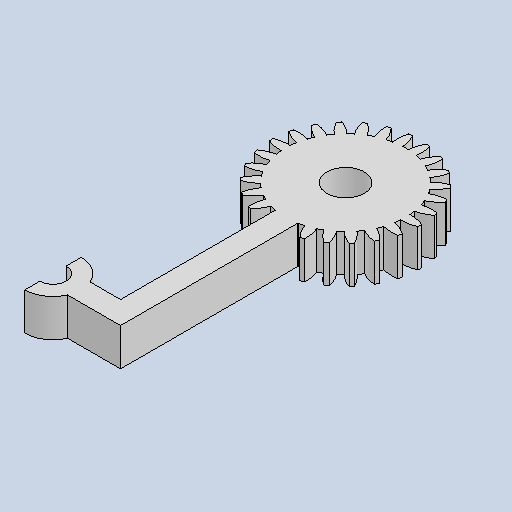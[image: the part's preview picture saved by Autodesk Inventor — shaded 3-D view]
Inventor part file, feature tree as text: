
AUTODESK INVENTOR PART (.ipt)
format: ipt  version: 2022 (Build 260153000, 153)  size: 292,352 bytes
history: native  units: in
note: dims shown in document units (in); Inventor stores cm internally (conversion verified against a paired STEP export)
features: extrude x6, sketch x6, pattern_circular x1
ambient origin geometry x8: Origin, YZ Plane, XZ Plane, XY Plane, X Axis, Y Axis, Z Axis, Center Point
bodies: Solid1 (feature_tree)
feature tree (13):
  extrude  "Extrusion1"  Depth=0.1575in
  pattern_circular  "Circular Pattern1"  [2 undecoded]
  extrude  "Extrusion6"  Depth=0.1969in TaperAngle=0.0deg
  extrude  "Extrusion10"  Depth=0.1969in TaperAngle=360.0deg
  extrude  "Extrusion11"  Depth=0.1969in
  extrude  "Extrusion12"  Depth=0.1969in
  extrude  "Extrusion13"  Depth=0.1969in TaperAngle=0.0deg
  sketch  "Sketch1"  dims[d0=0.6299in d1=0.1575in]
  sketch  "Sketch8"  dims[d2=0.0098in]
  sketch  "Sketch12"  dims[d3=0.0098in]
  sketch  "Sketch14"  dims[d4=0.0236in]
  sketch  "Sketch15"  dims[d7=0.0472in]
  sketch  "Sketch16"  dims[d8=0.1772in d10=0.0787in d11=0.1969in d12=0.0in d13=10.2362in d14=360.0deg d49=0.1969in d50=0.1575in d51=0.5438in d52=0.0in d89=0.0591in d90=0.0591in d91=0.3937in d92=0.0in d93=0.3937in d94=0.0in d95=0.3543in d96=1.1811in d97=0.1181in d98=0.0591in d99=0.0591in d100=0.1378in d101=0.1969in d102=0.1969in d103=0.0in d104=0.0787in d105=0.0787in d106=0.2953in d107=0.1969in d108=0.1969in d109=0.0in d69=0.0197in d70=0.0344in d71=0.0197in d72=0.0344in]
note: 2 required parameter values undecoded (feature->parameter linkage not recoverable at this tier; creation-order binding heuristic only, values carry confidence <= 0.55)
